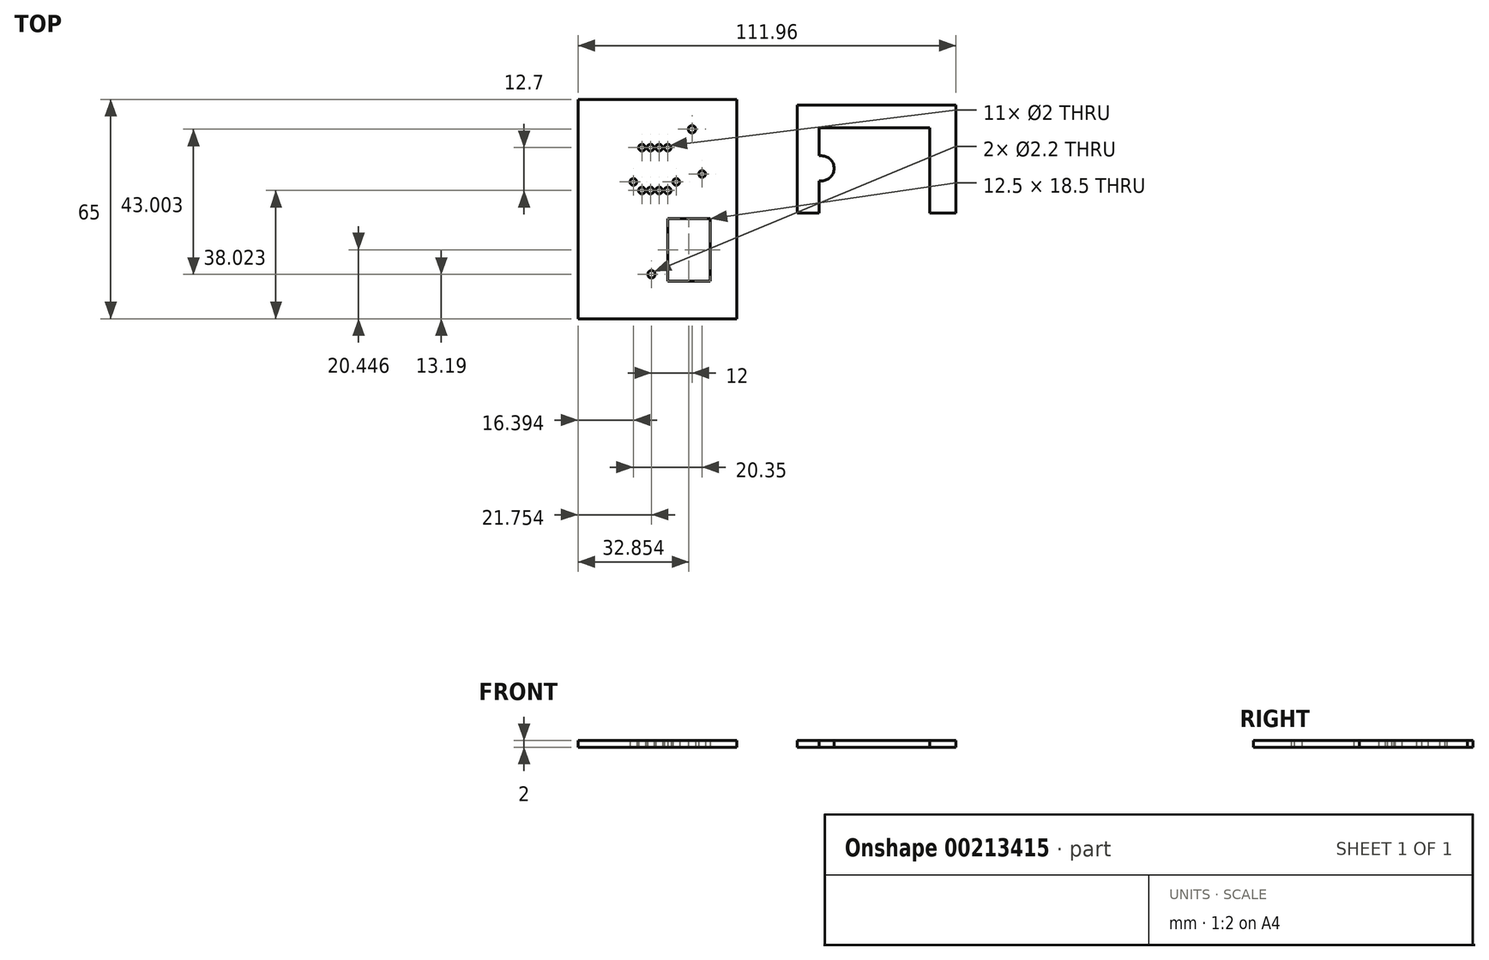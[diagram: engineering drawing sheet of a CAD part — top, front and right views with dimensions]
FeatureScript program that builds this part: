
annotation { "Feature Type Name" : "Feature", "Feature Type Description" : "" }
export const myFeature = defineFeature(function(context is Context, id is Id, definition is map)
    precondition{}
    {
        {
            var Q0;
            Q0=qCreatedBy(makeId("Top.planeOp"),FACE);
            var sketch = newSketch(context, id + "F0", { "sketchPlane" : qUnion([Q0])});
            skLineSegment(sketch, "E0.bottom", {"start": v(-108.39, 16.28) * mm, "end": v(-61.39, 16.28) * mm});
            skLineSegment(sketch, "E0.top", {"start": v(-108.39, -48.72) * mm, "end": v(-61.39, -48.72) * mm});
            skLineSegment(sketch, "E0.left", {"start": v(-108.39, 16.28) * mm, "end": v(-108.39, -48.72) * mm});
            skLineSegment(sketch, "E0.right", {"start": v(-61.39, 16.28) * mm, "end": v(-61.39, -48.72) * mm});
            skLineSegment(sketch, "E1", {"start": v(-43.43, -17.32) * mm, "end": v(-43.43, 14.68) * mm});
            skLineSegment(sketch, "E2", {"start": v(-43.43, 14.68) * mm, "end": v(3.57, 14.68) * mm});
            skLineSegment(sketch, "E3", {"start": v(3.57, 14.68) * mm, "end": v(3.57, -17.32) * mm});
            skLineSegment(sketch, "E4", {"start": v(3.57, -17.32) * mm, "end": v(-4.23, -17.32) * mm});
            skLineSegment(sketch, "E5", {"start": v(-4.23, -17.32) * mm, "end": v(-4.23, 7.88) * mm});
            skLineSegment(sketch, "E6", {"start": v(-4.23, 7.88) * mm, "end": v(-37.03, 7.88) * mm});
            skLineSegment(sketch, "E7", {"start": v(-37.03, 7.88) * mm, "end": v(-37.03, -0.42) * mm});
            skLineSegment(sketch, "E8", {"start": v(-37.03, -17.32) * mm, "end": v(-43.43, -17.32) * mm});
            skCircle(sketch, "E9", {"center": v(-89.46, -10.7) * mm, "radius": 1 * mm});
            skCircle(sketch, "E10", {"center": v(-86.92, -10.7) * mm, "radius": 1 * mm});
            skCircle(sketch, "E11", {"center": v(-84.38, -10.7) * mm, "radius": 1 * mm});
            skCircle(sketch, "E12", {"center": v(-81.84, -10.7) * mm, "radius": 1 * mm});
            skCircle(sketch, "E13", {"center": v(-79.3, -8.16) * mm, "radius": 1 * mm});
            skCircle(sketch, "E14", {"center": v(-92, -8.16) * mm, "radius": 1 * mm});
            skCircle(sketch, "E15", {"center": v(-89.46, 2) * mm, "radius": 1 * mm});
            skCircle(sketch, "E16", {"center": v(-86.92, 2) * mm, "radius": 1 * mm});
            skCircle(sketch, "E17", {"center": v(-84.38, 2) * mm, "radius": 1 * mm});
            skCircle(sketch, "E18", {"center": v(-81.84, 2) * mm, "radius": 1 * mm});
            skCircle(sketch, "E19", {"center": v(-71.65, -5.78) * mm, "radius": 1 * mm});
            skArc(sketch, "E20", {"start": v(-36.23, -0.42) * mm, "mid": v(-32.53, -4.12) * mm, "end": v(-36.23, -7.82) * mm});
            skLineSegment(sketch, "E21", {"start": v(-36.23, -0.42) * mm, "end": v(-37.03, -0.42) * mm});
            skLineSegment(sketch, "E22", {"start": v(-36.23, -7.82) * mm, "end": v(-37.03, -7.82) * mm});
            skLineSegment(sketch, "E23.trimOffspring", {"start": v(-37.03, -7.82) * mm, "end": v(-37.03, -17.32) * mm});
            skLineSegment(sketch, "E24", {"start": v(-101.89, 9.48) * mm, "end": v(-101.89, -37.52) * mm, "construction": true});
            skLineSegment(sketch, "E25", {"start": v(-101.89, -37.52) * mm, "end": v(-69.29, -37.52) * mm, "construction": true});
            skLineSegment(sketch, "E26", {"start": v(-69.29, -37.52) * mm, "end": v(-69.29, 9.48) * mm, "construction": true});
            skLineSegment(sketch, "E27", {"start": v(-69.29, 9.48) * mm, "end": v(-101.89, 9.48) * mm, "construction": true});
            skCircle(sketch, "E28", {"center": v(-74.64, 7.47) * mm, "radius": 1.1 * mm});
            skCircle(sketch, "E29", {"center": v(-86.64, -35.53) * mm, "radius": 1.1 * mm});
            skLineSegment(sketch, "E30.bottom", {"start": v(-69.29, -37.52) * mm, "end": v(-81.79, -37.52) * mm});
            skLineSegment(sketch, "E30.top", {"start": v(-69.29, -19.02) * mm, "end": v(-81.79, -19.02) * mm});
            skLineSegment(sketch, "E30.left", {"start": v(-69.29, -37.52) * mm, "end": v(-69.29, -19.02) * mm});
            skLineSegment(sketch, "E30.right", {"start": v(-81.79, -37.52) * mm, "end": v(-81.79, -19.02) * mm});
            skSolve(sketch);
        }
        {
            var Q0;
            Q0=makeQuery(id+"F0.imprint","IMPRINT",FACE,{"disambiguationData":[TD([[makeQuery(id+"F0.imprint","IMPRINT",EDGE,{"derivedFrom":sQuery(id+"F0.wireOp",EDGE,"E0.bottom")}),-1.0]])]});
            extrude(context, id + "F1", {"entities" : qUnion([Q0]), "depth" : 2 * mm});
        }
        {
            var Q0;
            Q0=makeQuery(id+"F0.imprint","IMPRINT",FACE,{"disambiguationData":[TD([[makeQuery(id+"F0.imprint","IMPRINT",EDGE,{"derivedFrom":sQuery(id+"F0.wireOp",EDGE,"E1")}),-1.0]])]});
            extrude(context, id + "F2", {"entities" : qUnion([Q0]), "depth" : 2 * mm});
        }
    });
